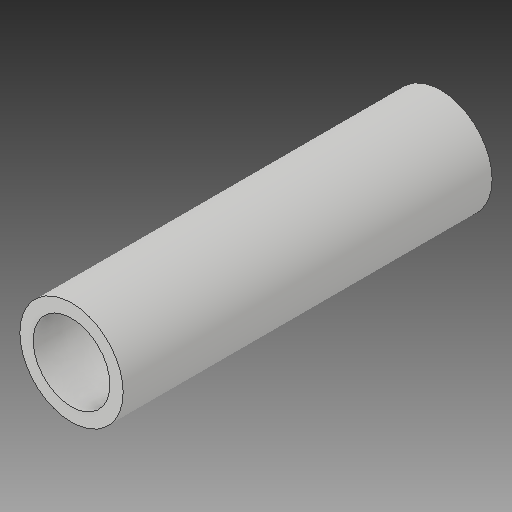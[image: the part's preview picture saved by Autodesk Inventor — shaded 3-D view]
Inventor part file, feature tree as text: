
AUTODESK INVENTOR PART (.ipt)
format: ipt  version: 2018 (Build 220112000, 112)  size: 100,352 bytes
history: native  units: mm
features: other x3, sketch x1
ambient origin geometry x8: Origin, YZ Plane, XZ Plane, XY Plane, X Axis, Y Axis, Z Axis, Center Point
bodies: Solid1 (feature_tree)
feature tree (4):
  other  "25mmspacer.ipt"
  other  "Solid1::25mmspacer.ipt"
  other  "TaggingFeature1"
  sketch  "Sketch1"  dims[d0=10.0mm]
